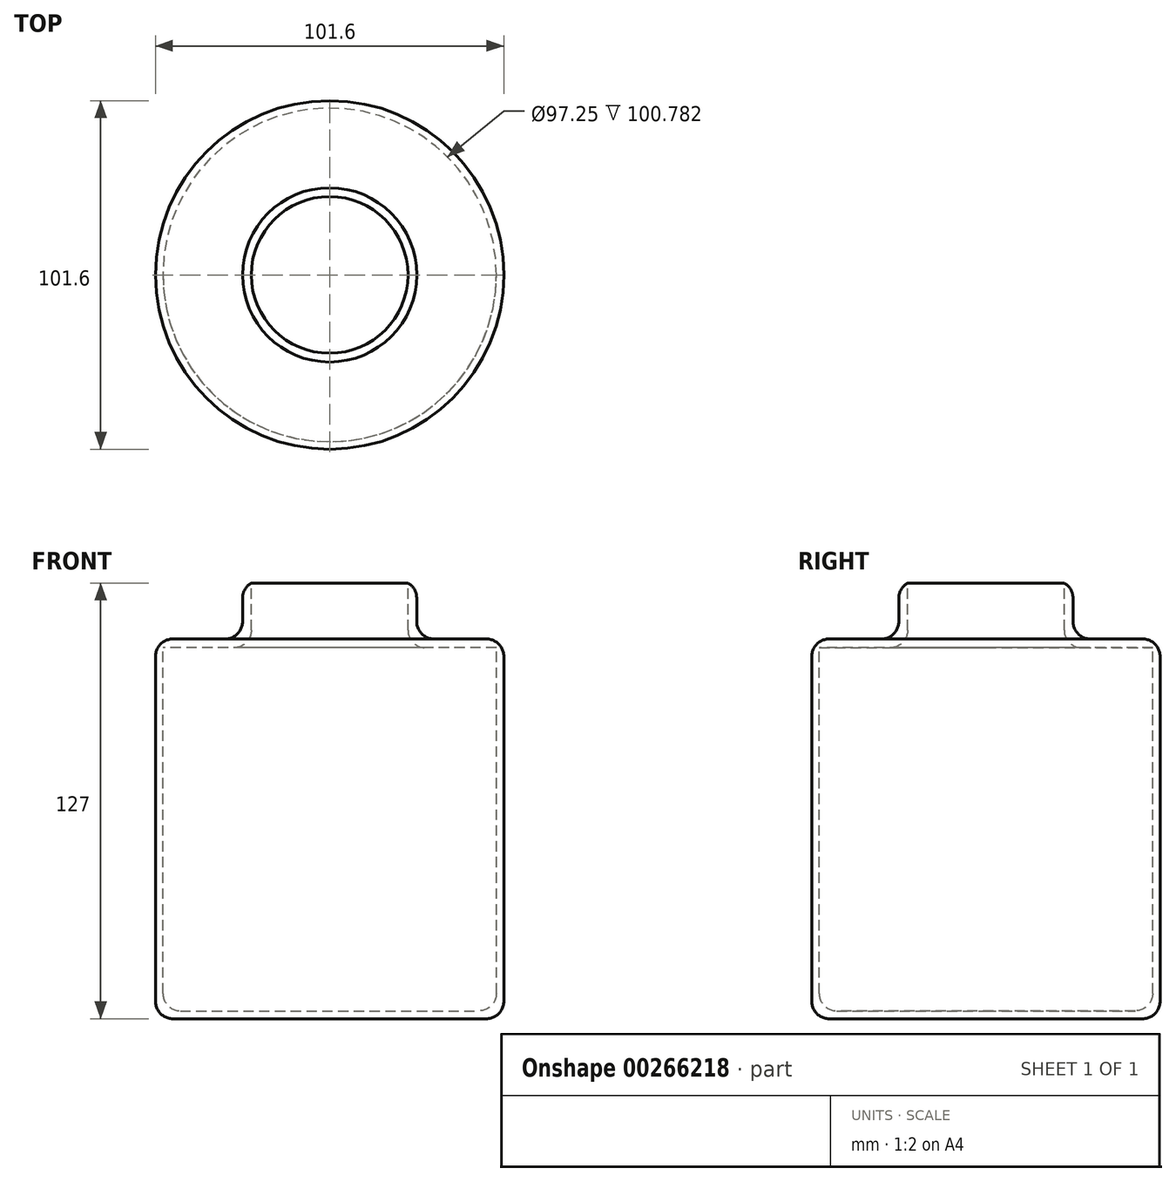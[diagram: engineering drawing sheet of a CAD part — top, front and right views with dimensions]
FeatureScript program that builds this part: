
annotation { "Feature Type Name" : "Feature", "Feature Type Description" : "" }
export const myFeature = defineFeature(function(context is Context, id is Id, definition is map)
    precondition{}
    {
        {
            var Q0;
            Q0=qCreatedBy(makeId("Front.planeOp"),FACE);
            var sketch = newSketch(context, id + "F0", { "sketchPlane" : qUnion([Q0])});
            skLineSegment(sketch, "E0", {"start": v(0, 63.5) * mm, "end": v(0, 0) * mm});
            skLineSegment(sketch, "E1", {"start": v(0, 0) * mm, "end": v(0, -63.5) * mm});
            skLineSegment(sketch, "E2", {"start": v(0, -63.5) * mm, "end": v(50.8, -63.5) * mm});
            skLineSegment(sketch, "E3", {"start": v(50.8, -63.5) * mm, "end": v(50.8, 47.18) * mm});
            skLineSegment(sketch, "E4", {"start": v(50.8, 47.18) * mm, "end": v(25.4, 47.18) * mm});
            skLineSegment(sketch, "E5", {"start": v(25.4, 47.18) * mm, "end": v(25.4, 62.8) * mm});
            skLineSegment(sketch, "E6", {"start": v(0, 63.5) * mm, "end": v(25.4, 63.5) * mm});
            skLineSegment(sketch, "E7", {"start": v(25.4, 63.5) * mm, "end": v(25.4, 47.18) * mm});
            skLineSegment(sketch, "E8", {"start": v(22.84, 63.5) * mm, "end": v(22.84, 44.64) * mm});
            skLineSegment(sketch, "E9", {"start": v(22.84, 44.64) * mm, "end": v(48.63, 44.64) * mm});
            skLineSegment(sketch, "E10", {"start": v(48.63, 44.64) * mm, "end": v(48.63, -61.22) * mm});
            skLineSegment(sketch, "E11", {"start": v(48.63, -61.22) * mm, "end": v(1.95, -61.22) * mm});
            skLineSegment(sketch, "E12", {"start": v(1.95, -61.22) * mm, "end": v(0, -61.22) * mm});
            skSolve(sketch);
        }
        {
            var Q0;
            {var subQ5=sQuery(id+"F0.wireOp",EDGE,"E2");Q0=makeQuery(id+"F0.imprint","IMPRINT",FACE,{"disambiguationData":[TD([[makeQuery(id+"F0.imprint","IMPRINT",EDGE,{"derivedFrom":subQ5}),1.0]])]});}
            var Q1;
            Q1=sQuery(id+"F0.wireOp",EDGE,"E1");
            revolve(context, id + "F1", {"entities" : qUnion([Q0]), "axis" : qUnion([Q1]), "revolveType" : RevolveType.FULL});
        }
        {
            var Q0;
            Q0=makeQuery(id+"F1.opRevolve","SWEPT_EDGE",EDGE,{"disambiguationData":[OSD([sQuery(id+"F0.wireOp",EDGE,"E6"),sQuery(id+"F0.wireOp",EDGE,"E7")])]});
            var Q1;
            Q1=makeQuery(id+"F1.opRevolve","SWEPT_EDGE",EDGE,{"disambiguationData":[OSD([sQuery(id+"F0.wireOp",EDGE,"E4"),sQuery(id+"F0.wireOp",EDGE,"E7")])]});
            var Q2;
            Q2=makeQuery(id+"F1.opRevolve","SWEPT_EDGE",EDGE,{"disambiguationData":[OSD([sQuery(id+"F0.wireOp",EDGE,"E3"),sQuery(id+"F0.wireOp",EDGE,"E4")])]});
            var Q3;
            Q3=makeQuery(id+"F1.opRevolve","SWEPT_FACE",FACE,{"disambiguationData":[OSD([sQuery(id+"F0.wireOp",EDGE,"E4")])]});
            var Q4;
            Q4=makeQuery(id+"F1.opRevolve","SWEPT_FACE",FACE,{"disambiguationData":[OSD([sQuery(id+"F0.wireOp",EDGE,"E3")])]});
            var Q5;
            Q5=makeQuery(id+"F1.opRevolve","SWEPT_EDGE",EDGE,{"disambiguationData":[OSD([sQuery(id+"F0.wireOp",EDGE,"E2"),sQuery(id+"F0.wireOp",EDGE,"E3")])]});
            var Q6;
            Q6=makeQuery(id+"F1.opRevolve","SWEPT_FACE",FACE,{"disambiguationData":[OSD([sQuery(id+"F0.wireOp",EDGE,"E2")])]});
            var Q7;
            Q7=makeQuery(id+"F1.opRevolve","SWEPT_EDGE",EDGE,{"disambiguationData":[OSD([sQuery(id+"F0.wireOp",EDGE,"E10"),sQuery(id+"F0.wireOp",EDGE,"E11")])]});
            var Q8;
            Q8=makeQuery(id+"F1.opRevolve","SWEPT_EDGE",EDGE,{"disambiguationData":[OSD([sQuery(id+"F0.wireOp",EDGE,"E8"),sQuery(id+"F0.wireOp",EDGE,"E9")])]});
            fillet(context, id + "F2", {"entities" : qUnion([Q0, Q1, Q2, Q3, Q4, Q5, Q6, Q7, Q8]), "radius" : 5.08 * mm, "tangentPropagation" : true, "allowEdgeOverflow" : false});
        }
    });
